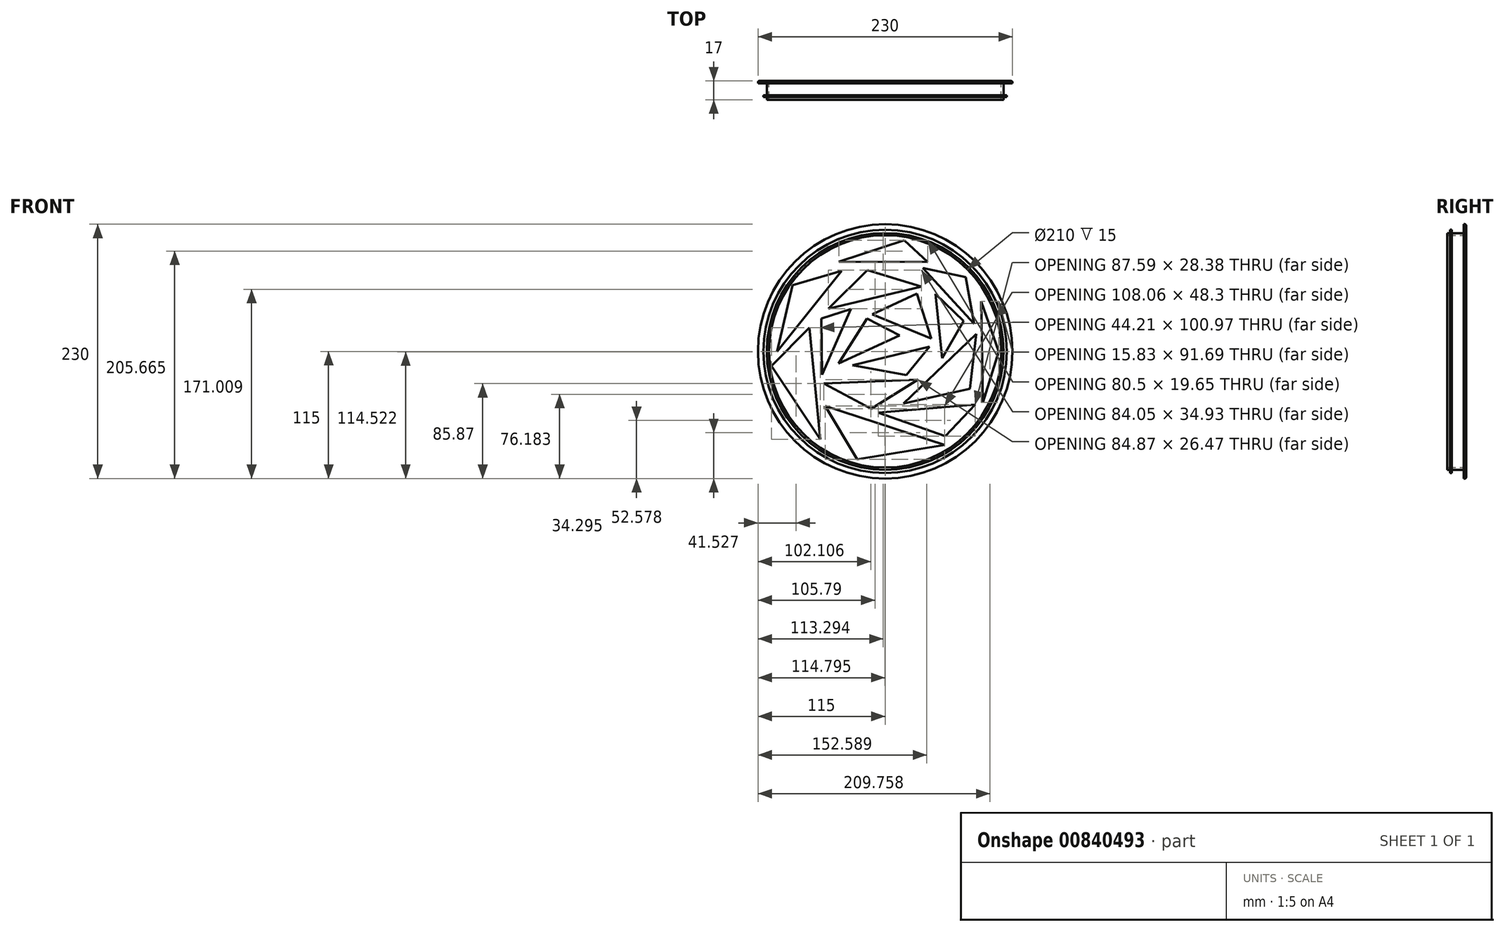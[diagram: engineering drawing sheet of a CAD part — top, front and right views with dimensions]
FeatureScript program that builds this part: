
annotation { "Feature Type Name" : "Feature", "Feature Type Description" : "" }
export const myFeature = defineFeature(function(context is Context, id is Id, definition is map)
    precondition{}
    {
        {
            var Q0;
            Q0=qCreatedBy(makeId("Front.planeOp"),FACE);
            var sketch = newSketch(context, id + "F0", { "sketchPlane" : qUnion([Q0])});
            skCircle(sketch, "E0", {"center": v(0, 0) * mm, "radius": 115 * mm});
            skSolve(sketch);
        }
        {
            var Q0;
            Q0 = qSketchRegion(id + "F0", true);
            extrude(context, id + "F1", {"entities" : qUnion([Q0]), "depth" : 2 * mm, "offsetDistance" : 25 * mm});
        }
        {
            var Q0;
            Q0=makeQuery(id+"F1.opExtrude","CAP_FACE",FACE,{"disambiguationData":[OSD([sQuery(id+"F0.wireOp",EDGE,"E0")])],"isStart":false});
            var sketch = newSketch(context, id + "F2", { "sketchPlane" : qUnion([Q0])});
            skCircle(sketch, "E1", {"center": v(0, 0) * mm, "radius": 105 * mm});
            skCircle(sketch, "E2.0", {"center": v(0, 0) * mm, "radius": 107 * mm});
            skSolve(sketch);
        }
        {
            var Q0;
            Q0 = qSketchRegion(id + "F2", true);
            extrude(context, id + "F3", {"entities" : qUnion([Q0]), "operationType" : NewBodyOperationType.ADD, "depth" : 15 * mm, "offsetDistance" : 25 * mm});
        }
        {
            var Q0;
            {var subQ0=sQuery(id+"F0.wireOp",EDGE,"E0");Q0=makeQuery(id+"F3.boolean.opBoolean","SPLIT",FACE,{"disambiguationData":[TD([makeQuery(id+"F1.opExtrude","SWEPT_FACE",FACE,{"disambiguationData":[OSD([subQ0])]})])],"derivedFrom":makeQuery(id+"F1.opExtrude","CAP_FACE",FACE,{"disambiguationData":[OSD([subQ0])],"isStart":false})});}
            cPlane(context, id + "F4", {"entities" : qUnion([Q0]), "cplaneType" : CPlaneType.OFFSET, "offset" : 11 * mm, "width" : 150 * mm, "height" : 150 * mm});
        }
        {
            var Q0;
            Q0=qCreatedBy(id+"F4.planeOp",FACE);
            var sketch = newSketch(context, id + "F5", { "sketchPlane" : qUnion([Q0])});
            skCircle(sketch, "E3", {"center": v(0, 0) * mm, "radius": 110 * mm});
            skSolve(sketch);
        }
        {
            var Q0;
            Q0 = qSketchRegion(id + "F5", true);
            extrude(context, id + "F6", {"entities" : qUnion([Q0]), "operationType" : NewBodyOperationType.ADD, "depth" : 1.5 * mm, "offsetDistance" : 25 * mm});
        }
        {
            var Q0;
            Q0=makeQuery(id+"F1.opExtrude","CAP_FACE",FACE,{"disambiguationData":[OSD([sQuery(id+"F0.wireOp",EDGE,"E0")])],"isStart":true});
            fillet(context, id + "F7", {"entities" : qUnion([Q0]), "radius" : 1 * mm, "tangentPropagation" : true, "allowEdgeOverflow" : false});
        }
        {
            var Q0;
            Q0=qCreatedBy(id+"F4.planeOp",FACE);
            var sketch = newSketch(context, id + "F8", { "sketchPlane" : qUnion([Q0])});
            skCircle(sketch, "E4", {"center": v(0, 0) * mm, "radius": 103.94 * mm});
            skSolve(sketch);
        }
        {
            var Q0;
            Q0=makeQuery(id+"F6.boolean.opBoolean","SPLIT",FACE,{"disambiguationData":[TD([makeQuery(id+"F3.opExtrude","SWEPT_FACE",FACE,{"disambiguationData":[OSD([sQuery(id+"F2.wireOp",EDGE,"E1")])]})])],"derivedFrom":makeQuery(id+"F6.opExtrude","CAP_FACE",FACE,{"disambiguationData":[OSD([sQuery(id+"F5.wireOp",EDGE,"E3")])],"isStart":false})});
            var Q1;
            Q1=sQuery(id+"F8.wireOp",EDGE,"E4");
            extrude(context, id + "F9", {"entities" : qUnion([Q0]), "operationType" : NewBodyOperationType.REMOVE, "surfaceEntities" : qUnion([Q1]), "oppositeDirection" : true, "depth" : 12 * mm, "offsetDistance" : 25 * mm});
        }
        {
            var Q0;
            Q0=makeQuery(id+"F1.opExtrude","CAP_FACE",FACE,{"disambiguationData":[OSD([sQuery(id+"F0.wireOp",EDGE,"E0")])],"isStart":true});
            var sketch = newSketch(context, id + "F10", { "sketchPlane" : qUnion([Q0])});
            skLineSegment(sketch, "E5", {"start": v(-38.54, 80.84) * mm, "end": v(-17.26, 100.49) * mm});
            skLineSegment(sketch, "E6", {"start": v(-17.26, 100.49) * mm, "end": v(41.96, 81.11) * mm});
            skLineSegment(sketch, "E7", {"start": v(41.96, 81.11) * mm, "end": v(-38.54, 80.84) * mm});
            skLineSegment(sketch, "E8", {"start": v(39.23, 72.93) * mm, "end": v(83.7, 59.83) * mm});
            skLineSegment(sketch, "E9", {"start": v(83.7, 59.83) * mm, "end": v(97.62, 0) * mm});
            skLineSegment(sketch, "E10", {"start": v(97.62, 0) * mm, "end": v(39.23, 72.93) * mm});
            skLineSegment(sketch, "E11", {"start": v(68.42, 21.35) * mm, "end": v(102.8, -13.3) * mm});
            skLineSegment(sketch, "E12", {"start": v(102.8, -13.3) * mm, "end": v(58.6, -79.61) * mm});
            skLineSegment(sketch, "E13", {"start": v(58.6, -79.61) * mm, "end": v(68.42, 21.35) * mm});
            skLineSegment(sketch, "E14", {"start": v(54.24, -49.32) * mm, "end": v(25.3, -97.62) * mm});
            skLineSegment(sketch, "E15", {"start": v(25.3, -97.62) * mm, "end": v(-53.83, -84.52) * mm});
            skLineSegment(sketch, "E16", {"start": v(-53.83, -84.52) * mm, "end": v(54.24, -49.32) * mm});
            skLineSegment(sketch, "E17", {"start": v(-54.37, -76.61) * mm, "end": v(6.2, -55.33) * mm});
            skLineSegment(sketch, "E18", {"start": v(6.2, -55.33) * mm, "end": v(-81.39, -48.23) * mm});
            skLineSegment(sketch, "E19", {"start": v(-81.39, -48.23) * mm, "end": v(-54.37, -76.61) * mm});
            skLineSegment(sketch, "E20", {"start": v(-88.48, -46.32) * mm, "end": v(-102.67, 0) * mm});
            skLineSegment(sketch, "E21", {"start": v(-102.67, 0) * mm, "end": v(-86.84, 45.37) * mm});
            skLineSegment(sketch, "E22", {"start": v(-86.84, 45.37) * mm, "end": v(-88.48, -46.32) * mm});
            skLineSegment(sketch, "E23", {"start": v(-72.65, 67.2) * mm, "end": v(-33.9, 75.38) * mm});
            skLineSegment(sketch, "E24", {"start": v(-33.9, 75.38) * mm, "end": v(-80.57, 24.9) * mm});
            skLineSegment(sketch, "E25", {"start": v(-80.57, 24.9) * mm, "end": v(-72.65, 67.2) * mm});
            skSolve(sketch);
        }
        {
            var Q0;
            Q0 = qSketchRegion(id + "F10", true);
            extrude(context, id + "F11", {"entities" : qUnion([Q0]), "operationType" : NewBodyOperationType.REMOVE, "oppositeDirection" : true, "depth" : 15 * mm, "offsetDistance" : 25 * mm});
        }
        {
            var Q0;
            Q0=makeQuery(id+"F1.opExtrude","CAP_FACE",FACE,{"disambiguationData":[OSD([sQuery(id+"F0.wireOp",EDGE,"E0")])],"isStart":true});
            var sketch = newSketch(context, id + "F12", { "sketchPlane" : qUnion([Q0])});
            skLineSegment(sketch, "E26", {"start": v(-32.81, 58.74) * mm, "end": v(16.03, 73.47) * mm});
            skLineSegment(sketch, "E27", {"start": v(16.03, 73.47) * mm, "end": v(51.23, 38.54) * mm});
            skLineSegment(sketch, "E28", {"start": v(51.23, 38.54) * mm, "end": v(-32.81, 58.74) * mm});
            skLineSegment(sketch, "E29", {"start": v(31.04, 38.27) * mm, "end": v(57.78, 29.54) * mm});
            skLineSegment(sketch, "E30", {"start": v(57.78, 29.54) * mm, "end": v(56.96, -21.22) * mm});
            skLineSegment(sketch, "E31", {"start": v(56.96, -21.22) * mm, "end": v(31.04, 38.27) * mm});
            skLineSegment(sketch, "E32", {"start": v(55.33, -29.13) * mm, "end": v(12.48, -52.05) * mm});
            skLineSegment(sketch, "E33", {"start": v(12.48, -52.05) * mm, "end": v(-29.54, -25.58) * mm});
            skLineSegment(sketch, "E34", {"start": v(-29.54, -25.58) * mm, "end": v(55.33, -29.13) * mm});
            skLineSegment(sketch, "E35", {"start": v(-16.71, -47.14) * mm, "end": v(-82.2, 15.62) * mm});
            skLineSegment(sketch, "E36", {"start": v(-82.2, 15.62) * mm, "end": v(-76.47, -33.77) * mm});
            skLineSegment(sketch, "E37", {"start": v(-76.47, -33.77) * mm, "end": v(-16.71, -47.14) * mm});
            skLineSegment(sketch, "E38", {"start": v(-45.37, 51.92) * mm, "end": v(-70.74, 27.63) * mm});
            skLineSegment(sketch, "E39", {"start": v(-70.74, 27.63) * mm, "end": v(-51.37, -6.2) * mm});
            skLineSegment(sketch, "E40", {"start": v(-51.37, -6.2) * mm, "end": v(-45.37, 51.92) * mm});
            skLineSegment(sketch, "E41", {"start": v(-28.72, 52.19) * mm, "end": v(11.67, 33.36) * mm});
            skLineSegment(sketch, "E42", {"start": v(11.67, 33.36) * mm, "end": v(-41.55, 11.53) * mm});
            skLineSegment(sketch, "E43", {"start": v(-41.55, 11.53) * mm, "end": v(-28.72, 52.19) * mm});
            skLineSegment(sketch, "E44", {"start": v(16.58, 29.81) * mm, "end": v(42.23, -10.85) * mm});
            skLineSegment(sketch, "E45", {"start": v(42.23, -10.85) * mm, "end": v(-13.17, 14.53) * mm});
            skLineSegment(sketch, "E46", {"start": v(-13.17, 14.53) * mm, "end": v(16.58, 29.81) * mm});
            skLineSegment(sketch, "E47", {"start": v(29.4, -12.48) * mm, "end": v(-40.18, 4.16) * mm});
            skLineSegment(sketch, "E48", {"start": v(-40.18, 4.16) * mm, "end": v(-19.17, -21.49) * mm});
            skLineSegment(sketch, "E49", {"start": v(-19.17, -21.49) * mm, "end": v(29.4, -12.48) * mm});
            skSolve(sketch);
        }
        {
            var Q0;
            Q0 = qSketchRegion(id + "F12", true);
            extrude(context, id + "F13", {"entities" : qUnion([Q0]), "operationType" : NewBodyOperationType.REMOVE, "oppositeDirection" : true, "depth" : 15 * mm, "offsetDistance" : 25 * mm});
        }
    });
